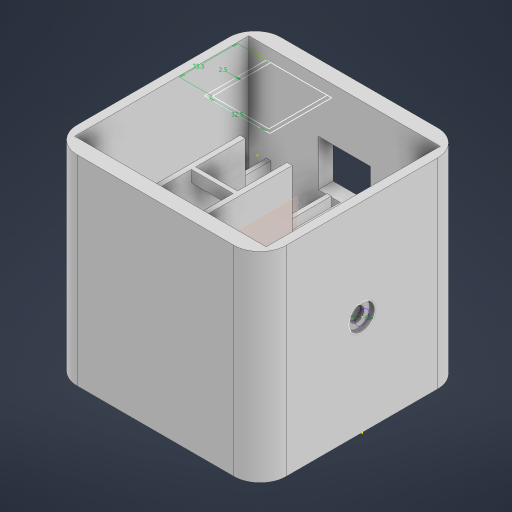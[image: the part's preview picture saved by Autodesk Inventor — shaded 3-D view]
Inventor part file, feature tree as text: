
AUTODESK INVENTOR PART (.ipt)
format: ipt  version: 2023 (Build 270158030, 158C)  size: 460,800 bytes
history: native  units: in
note: dims shown in document units (in); Inventor stores cm internally (conversion verified against a paired STEP export)
features: extrude x25, sketch x23, fillet x5, plane x2, loft x1
ambient origin geometry x8: Origin, YZ Plane, XZ Plane, XY Plane, X Axis, Y Axis, Z Axis, Center Point
bodies: Solid1 (feature_tree)
feature tree (56):
  extrude  "Extrusion1"  Depth=4.7244in
  sketch  "Sketch3"  dims[d2=2.3031in d3=2.3622in]
  extrude  "Extrusion3"  Depth=2.3622in
  loft  "Loft1"
  extrude  "Extrusion7"  Depth=2.2638in
  plane  "Work Plane2"
  extrude  "Extrusion8"  Depth=0.1969in
  plane  "Work Plane3"
  extrude  "Extrusion9"  Depth=0.3346in
  extrude  "Extrusion10"  Depth=4.3307in
  extrude  "Extrusion17"  Depth=1.5748in
  extrude  "Extrusion18"  Depth=1.5748in
  extrude  "Extrusion19"  Depth=1.1811in
  extrude  "Extrusion21"  TaperAngle=0.0deg  [1 undecoded]
  extrude  "Extrusion22"  Depth=1.1811in TaperAngle=0.0deg
  extrude  "Extrusion23"  Depth=2.5591in
  extrude  "Extrusion25"  TaperAngle=0.0deg  [1 undecoded]
  fillet  "Face Fillet1"
  sketch  "Sketch57"  dims[d119=1.1811in d120=2.2992in]
  extrude  "Extrusion26"  Depth=0.1181in
  extrude  "Extrusion27"  Depth=0.3346in TaperAngle=0.0deg
  sketch  "Sketch58"  dims[d121=0.0787in d123=1.1811in d124=0.0in]
  sketch  "Sketch59"  dims[d125=0.9055in d126=0.0787in]
  extrude  "Extrusion28"  Depth=2.2992in
  sketch  "Sketch60"  dims[d127=0.0984in d128=1.063in d129=0.0in]
  extrude  "Extrusion29"  Depth=1.1811in TaperAngle=0.0deg
  sketch  "Sketch61"  dims[d134=0.1378in d135=0.0in d136=0.0394in d137=0.0in]
  extrude  "Extrusion30"  Depth=0.0787in
  extrude  "Extrusion31"  Depth=1.063in TaperAngle=0.0deg
  extrude  "Extrusion32"  Depth=0.0394in TaperAngle=0.0deg
  extrude  "Extrusion33"  TaperAngle=0.0deg  [1 undecoded]
  extrude  "Extrusion34"  Depth=0.1969in
  extrude  "Extrusion35"  Depth=0.374in
  extrude  "Extrusion36"  TaperAngle=0.0deg  [1 undecoded]
  extrude  "Extrusion37"  Depth=1.7717in TaperAngle=0.0deg
  fillet  "Face Fillet2"
  fillet  "Face Fillet3"
  fillet  "Face Fillet4"
  fillet  "Face Fillet5"
  sketch  "Sketch2"  dims[d0=4.6063in d1=4.7244in]
  sketch  "Sketch4"  dims[d4=4.5276in d5=0.0in d6=0.315in]
  sketch  "Sketch13"  dims[d7=2.2638in d8=2.3031in]
  sketch  "Sketch14"  dims[d11=4.3307in d12=0.1969in]
  sketch  "Sketch18"  dims[d13=3.937in d14=0.3346in]
  sketch  "Sketch28"  dims[d15=4.3307in d16=0.0in d44=1.1024in]
  sketch  "Sketch31"  dims[d45=1.5748in d46=1.5748in]
  sketch  "Sketch32"  dims[d47=0.0in d48=1.5748in]
  sketch  "Sketch43"  dims[d49=1.5748in d50=1.1811in]
  sketch  "Sketch44"  dims[d51=0.0in d52=90.0deg d53=0.0in d54=90.0deg]
  sketch  "Sketch46"  dims[d57=1.7717in d58=1.1811in d59=0.0in]
  sketch  "Sketch49"  dims[d74=0.0in d75=2.5591in]
  sketch  "Sketch50"  dims[d76=0.1181in d77=0.0in d78=0.0in]
  sketch  "Sketch51"  dims[d79=0.1181in d80=0.0in d81=0.6063in]
  sketch  "Sketch54"  dims[d82=1.1811in d83=0.0in d117=0.3346in d118=0.0in]
  sketch  "Sketch62"  dims[d138=0.0in d139=0.0in]
  sketch  "Sketch63"  dims[d140=0.1181in d141=0.0in d148=0.1969in d150=0.374in d151=0.0in d152=1.7717in d153=0.0in d154=0.3937in d156=0.5906in d157=0.1969in d158=0.0in d159=0.1181in d160=0.0in d161=1.3976in d162=1.4764in d163=0.1969in d164=1.4764in d165=1.3976in d166=0.1969in d167=4.0551in d168=0.0in d169=1.2795in d170=0.0984in d171=1.3189in d172=4.0551in d173=0.0in d174=1.2795in d175=1.3189in d176=0.0984in d177=3.8976in d178=0.0in d179=1.9291in d180=0.0in d181=3.8976in d182=0.0in d183=1.9291in d184=0.0in d185=1.2795in d186=0.1969in d187=0.3543in d188=0.0in d189=1.2795in d190=0.1969in d191=0.3543in d192=0.0in d193=0.5906in d194=0.1969in d195=0.0in d196=0.1181in d197=0.0in d198=0.5906in d199=0.5906in d200=0.5906in d201=0.5906in d43=0.0in d87=0.0197in d88=0.0344in d89=0.0197in d90=0.0344in d144=0.0197in d145=0.0344in d146=0.0197in d147=0.0344in]
note: 4 required parameter values undecoded (feature->parameter linkage not recoverable at this tier; creation-order binding heuristic only, values carry confidence <= 0.55)
